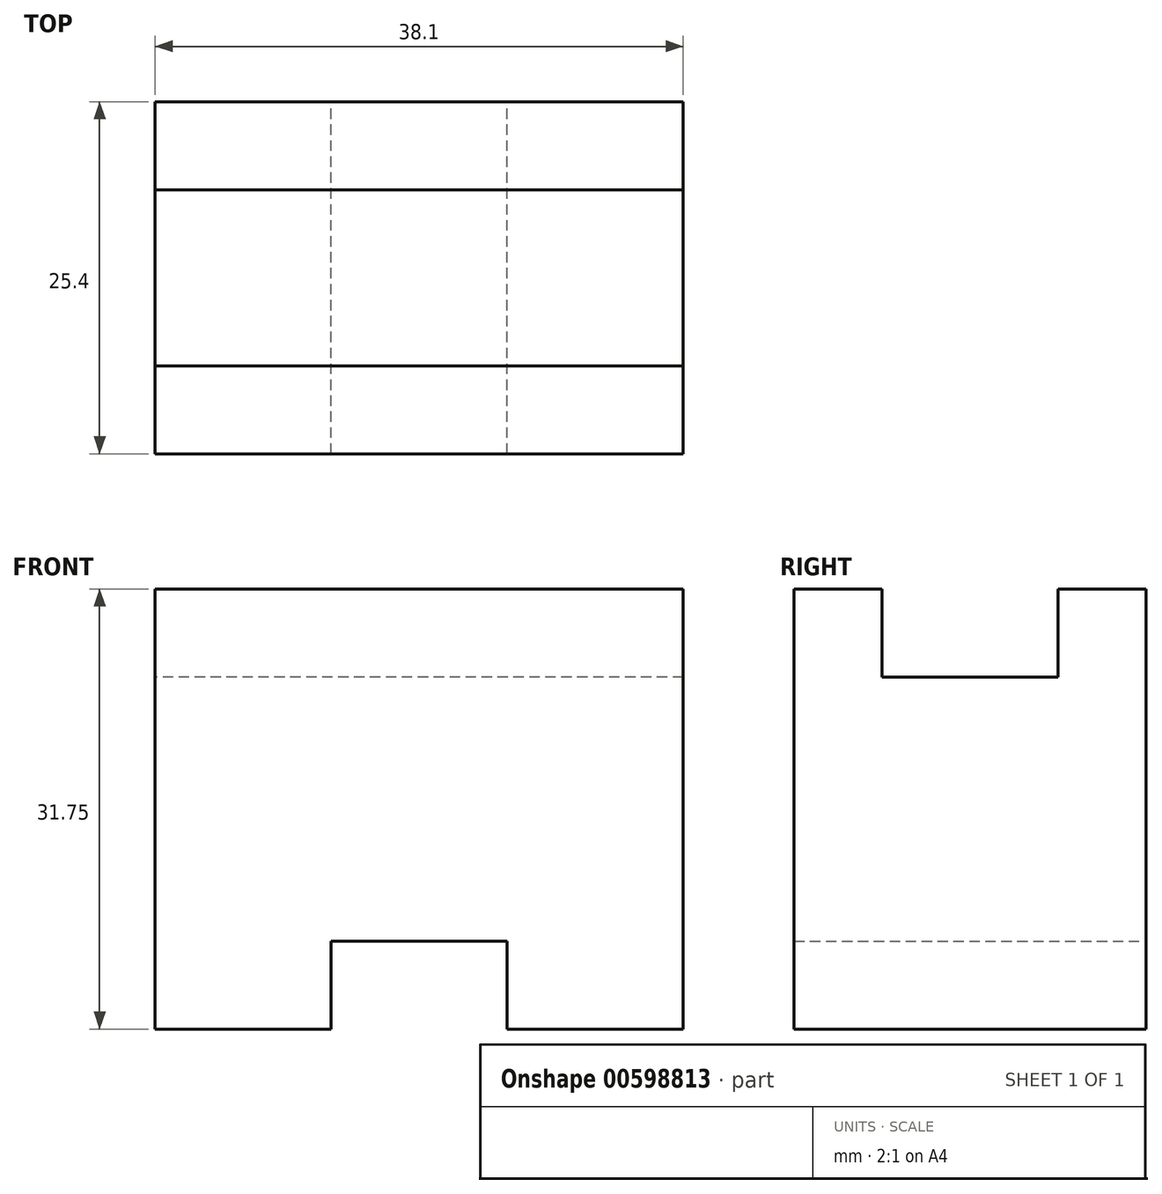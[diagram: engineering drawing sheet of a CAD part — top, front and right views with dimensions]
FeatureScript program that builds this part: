
annotation { "Feature Type Name" : "Feature", "Feature Type Description" : "" }
export const myFeature = defineFeature(function(context is Context, id is Id, definition is map)
    precondition{}
    {
        {
            var Q0;
            Q0=qCreatedBy(makeId("Front.planeOp"),FACE);
            var sketch = newSketch(context, id + "F0", { "sketchPlane" : qUnion([Q0])});
            skLineSegment(sketch, "E0", {"start": v(0, 0) * mm, "end": v(0, 31.75) * mm});
            skLineSegment(sketch, "E1", {"start": v(0, 31.75) * mm, "end": v(38.1, 31.75) * mm});
            skLineSegment(sketch, "E2", {"start": v(38.1, 31.75) * mm, "end": v(38.1, 0) * mm});
            skLineSegment(sketch, "E3", {"start": v(38.1, 0) * mm, "end": v(25.4, 0) * mm});
            skLineSegment(sketch, "E4", {"start": v(25.4, 0) * mm, "end": v(25.4, 6.35) * mm});
            skLineSegment(sketch, "E5", {"start": v(25.4, 6.35) * mm, "end": v(12.7, 6.35) * mm});
            skLineSegment(sketch, "E6", {"start": v(12.7, 6.35) * mm, "end": v(12.7, 0) * mm});
            skLineSegment(sketch, "E7", {"start": v(12.7, 0) * mm, "end": v(0, 0) * mm});
            skSolve(sketch);
        }
        {
            var Q0;
            Q0 = qSketchRegion(id + "F0", true);
            extrude(context, id + "F1", {"entities" : qUnion([Q0]), "depth" : 25.4 * mm, "offsetDistance" : 25.4 * mm});
        }
        {
            var Q0;
            Q0=makeQuery(id+"F1.opExtrude","SWEPT_FACE",FACE,{"disambiguationData":[OSD([sQuery(id+"F0.wireOp",EDGE,"E0")])]});
            var sketch = newSketch(context, id + "F2", { "sketchPlane" : qUnion([Q0])});
            skLineSegment(sketch, "E8", {"start": v(19.05, 31.75) * mm, "end": v(19.05, 25.4) * mm});
            skLineSegment(sketch, "E9", {"start": v(19.05, 25.4) * mm, "end": v(6.35, 25.4) * mm});
            skLineSegment(sketch, "E10", {"start": v(6.35, 25.4) * mm, "end": v(6.35, 31.75) * mm});
            skSolve(sketch);
        }
        {
            var Q0;
            Q0 = qSketchRegion(id + "F2", true);
            var Q1;
            {var subQ0=sQuery(id+"F2.wireOp",EDGE,"E8");Q1=makeQuery(id+"F2.imprint","IMPRINT",FACE,{"disambiguationData":[TD([[makeQuery(id+"F2.imprint","IMPRINT",EDGE,{"derivedFrom":subQ0}),-1.0]])]});}
            extrude(context, id + "F3", {"entities" : qUnion([Q0, Q1]), "operationType" : NewBodyOperationType.REMOVE, "oppositeDirection" : true, "depth" : 38.1 * mm, "offsetDistance" : 25.4 * mm});
        }
    });
